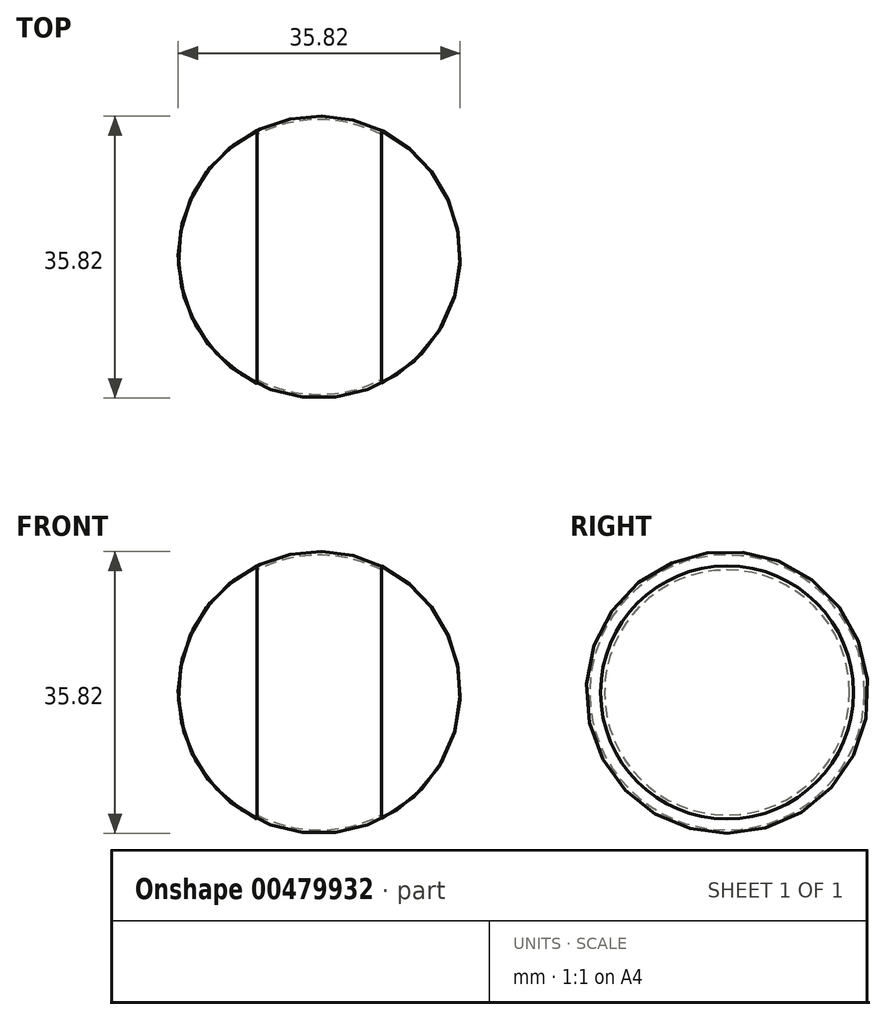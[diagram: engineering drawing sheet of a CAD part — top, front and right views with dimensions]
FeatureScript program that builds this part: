
annotation { "Feature Type Name" : "Feature", "Feature Type Description" : "" }
export const myFeature = defineFeature(function(context is Context, id is Id, definition is map)
    precondition{}
    {
        {
            var Q0;
            Q0=qCreatedBy(makeId("Front.planeOp"),FACE);
            var sketch = newSketch(context, id + "F0", { "sketchPlane" : qUnion([Q0])});
            skArc(sketch, "E0", {"start": v(7.91, 15.57) * mm, "mid": v(0, 17.46) * mm, "end": v(-7.9, 15.57) * mm});
            skLineSegment(sketch, "E1", {"start": v(-7.9, 15.57) * mm, "end": v(-7.9, 16.07) * mm, "construction": true});
            skLineSegment(sketch, "E2", {"start": v(7.72, 15.66) * mm, "end": v(7.9, 16.07) * mm, "construction": true});
            skArc(sketch, "E3", {"start": v(7.9, 16.07) * mm, "mid": v(0, 17.91) * mm, "end": v(-7.91, 16.07) * mm});
            skLineSegment(sketch, "E4", {"start": v(-7.9, 16.07) * mm, "end": v(-7.9, 15.57) * mm});
            skLineSegment(sketch, "E5", {"start": v(7.91, 16.07) * mm, "end": v(7.91, 15.57) * mm});
            skLineSegment(sketch, "E6", {"start": v(0, 0) * mm, "end": v(0, 17.46) * mm, "construction": true});
            skLineSegment(sketch, "E7", {"start": v(0, 17.46) * mm, "end": v(0, 17.91) * mm, "construction": true});
            skSolve(sketch);
        }
        {
            var Q0;
            Q0=qCreatedBy(makeId("Front.planeOp"),FACE);
            var sketch = newSketch(context, id + "F1", { "sketchPlane" : qUnion([Q0])});
            skLineSegment(sketch, "E8", {"start": v(-8.17, 0) * mm, "end": v(8.42, 0) * mm});
            skSolve(sketch);
        }
        {
            var Q0;
            Q0=qSketchRegion(id+"F0",true);
            var Q1;
            Q1=sQuery(id+"F1.wireOp",EDGE,"E8");
            revolve(context, id + "F2", {"entities" : qUnion([Q0]), "axis" : qUnion([Q1]), "revolveType" : RevolveType.FULL});
        }
    });
